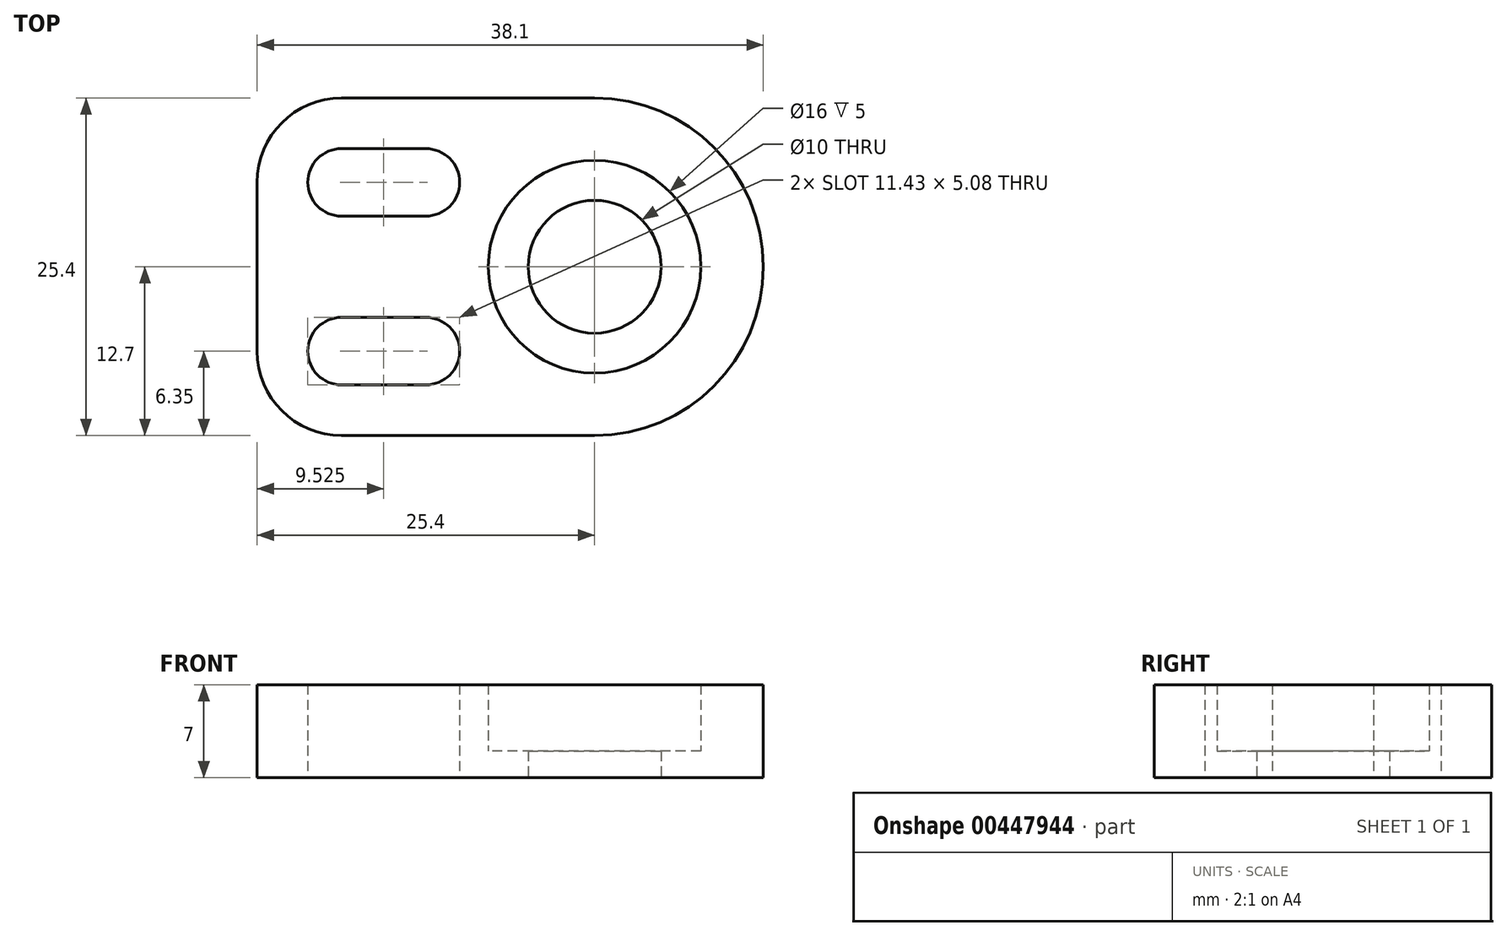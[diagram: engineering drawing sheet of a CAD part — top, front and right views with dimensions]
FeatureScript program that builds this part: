
annotation { "Feature Type Name" : "Feature", "Feature Type Description" : "" }
export const myFeature = defineFeature(function(context is Context, id is Id, definition is map)
    precondition{}
    {
        {
            var Q0;
            Q0=qCreatedBy(makeId("Top.planeOp"),FACE);
            var sketch = newSketch(context, id + "F0", { "sketchPlane" : qUnion([Q0])});
            skCircle(sketch, "E0", {"center": v(0, 0) * mm, "radius": 8 * mm});
            skArc(sketch, "E1", {"start": v(0, 12.7) * mm, "mid": v(12.7, 0) * mm, "end": v(0, -12.7) * mm});
            skLineSegment(sketch, "E2", {"start": v(-25.4, 6.35) * mm, "end": v(-25.4, -6.35) * mm});
            skLineSegment(sketch, "E3", {"start": v(0, 12.7) * mm, "end": v(-19.05, 12.7) * mm});
            skLineSegment(sketch, "E4", {"start": v(0, -12.7) * mm, "end": v(-19.05, -12.7) * mm});
            skArc(sketch, "E5", {"start": v(-25.4, -6.35) * mm, "mid": v(-23.54, -10.84) * mm, "end": v(-19.05, -12.7) * mm});
            skArc(sketch, "E6", {"start": v(-25.4, 6.35) * mm, "mid": v(-23.54, 10.84) * mm, "end": v(-19.05, 12.7) * mm});
            skLineSegment(sketch, "E7", {"start": v(-19.05, 6.35) * mm, "end": v(-12.7, 6.35) * mm, "construction": true});
            skLineSegment(sketch, "E8", {"start": v(-19.05, -6.35) * mm, "end": v(-12.7, -6.35) * mm, "construction": true});
            skArc(sketch, "E9.0.startCap", {"start": v(-19.05, 3.81) * mm, "mid": v(-21.6, 6.35) * mm, "end": v(-19.05, 8.9) * mm});
            skArc(sketch, "E9.0.endCap", {"start": v(-12.7, 8.9) * mm, "mid": v(-10.16, 6.35) * mm, "end": v(-12.7, 3.81) * mm});
            skLineSegment(sketch, "E9.0.left", {"start": v(-19.05, 8.9) * mm, "end": v(-12.7, 8.9) * mm});
            skLineSegment(sketch, "E9.0.right", {"start": v(-19.05, 3.81) * mm, "end": v(-12.7, 3.81) * mm});
            skArc(sketch, "E9.1.startCap", {"start": v(-19.05, -8.89) * mm, "mid": v(-21.6, -6.35) * mm, "end": v(-19.05, -3.8) * mm});
            skArc(sketch, "E9.1.endCap", {"start": v(-12.7, -3.8) * mm, "mid": v(-10.16, -6.35) * mm, "end": v(-12.7, -8.89) * mm});
            skLineSegment(sketch, "E9.1.left", {"start": v(-19.05, -3.8) * mm, "end": v(-12.7, -3.8) * mm});
            skLineSegment(sketch, "E9.1.right", {"start": v(-19.05, -8.89) * mm, "end": v(-12.7, -8.89) * mm});
            skSolve(sketch);
        }
        {
            var Q0;
            Q0=makeQuery(id+"F0.imprint","IMPRINT",FACE,{"disambiguationData":[TD([[makeQuery(id+"F0.imprint","IMPRINT",EDGE,{"derivedFrom":sQuery(id+"F0.wireOp",EDGE,"E0")}),-1.0]])]});
            extrude(context, id + "F1", {"entities" : qUnion([Q0]), "depth" : 7 * mm});
        }
        {
            var Q0;
            Q0=makeQuery(id+"F1.opExtrude","CAP_FACE",FACE,{"disambiguationData":[OSD([sQuery(id+"F0.wireOp",EDGE,"E0"),sQuery(id+"F0.wireOp",EDGE,"E1"),sQuery(id+"F0.wireOp",EDGE,"E2"),sQuery(id+"F0.wireOp",EDGE,"E3"),sQuery(id+"F0.wireOp",EDGE,"E4"),sQuery(id+"F0.wireOp",EDGE,"E5"),sQuery(id+"F0.wireOp",EDGE,"E6"),sQuery(id+"F0.wireOp",EDGE,"E9.0.startCap"),sQuery(id+"F0.wireOp",EDGE,"E9.0.endCap"),sQuery(id+"F0.wireOp",EDGE,"E9.0.left"),sQuery(id+"F0.wireOp",EDGE,"E9.0.right"),sQuery(id+"F0.wireOp",EDGE,"E9.1.startCap"),sQuery(id+"F0.wireOp",EDGE,"E9.1.endCap"),sQuery(id+"F0.wireOp",EDGE,"E9.1.left"),sQuery(id+"F0.wireOp",EDGE,"E9.1.right")])],"isStart":true});
            var sketch = newSketch(context, id + "F2", { "sketchPlane" : qUnion([Q0])});
            skCircle(sketch, "E10", {"center": v(0, 0) * mm, "radius": 5 * mm});
            skCircle(sketch, "E11.0", {"center": v(0, 0) * mm, "radius": 8 * mm});
            skSolve(sketch);
        }
        {
            var Q0;
            Q0=makeQuery(id+"F2.imprint","IMPRINT",FACE,{"disambiguationData":[TD([[makeQuery(id+"F2.imprint","IMPRINT",EDGE,{"derivedFrom":sQuery(id+"F2.wireOp",EDGE,"E10")}),-1.0]])]});
            extrude(context, id + "F3", {"entities" : qUnion([Q0]), "operationType" : NewBodyOperationType.ADD, "oppositeDirection" : true, "depth" : 2 * mm});
        }
    });
